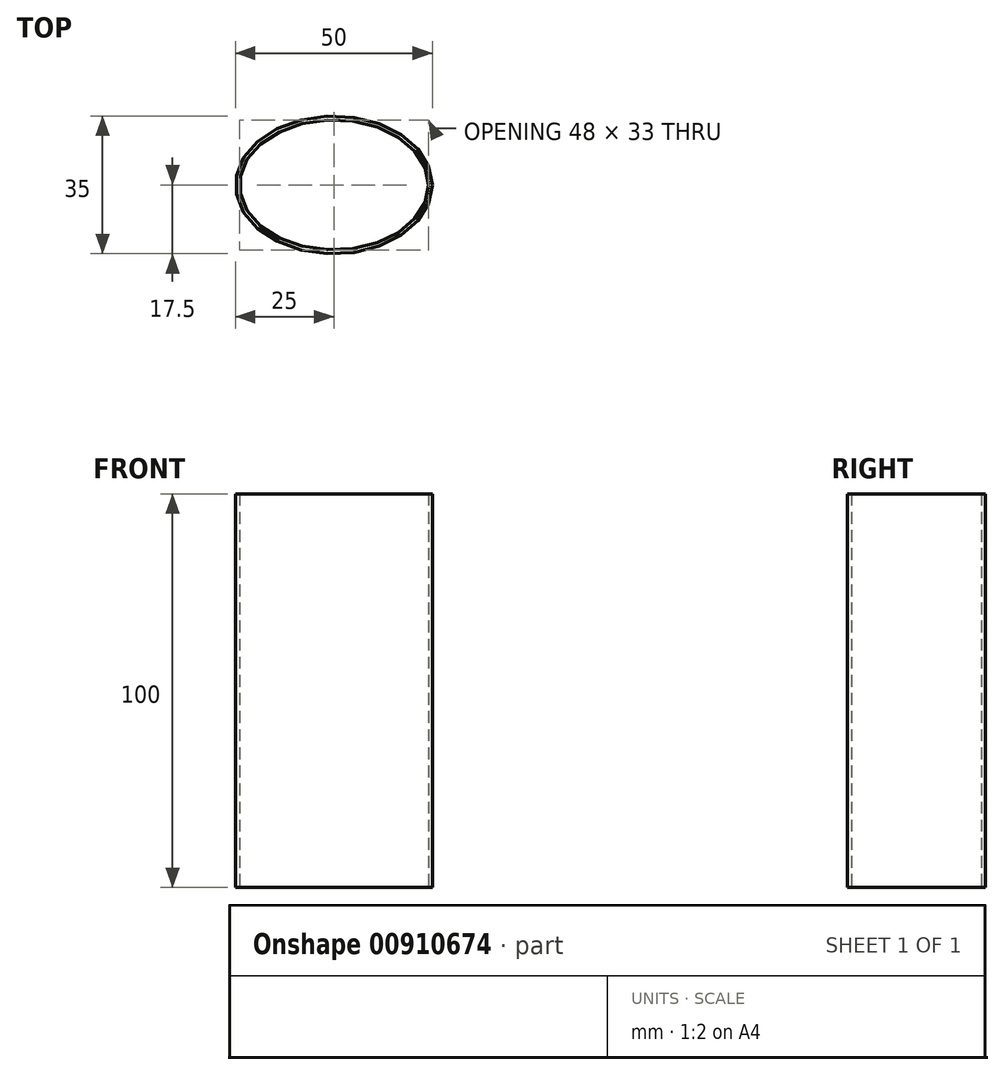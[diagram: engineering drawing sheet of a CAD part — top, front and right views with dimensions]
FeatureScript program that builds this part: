
annotation { "Feature Type Name" : "Feature", "Feature Type Description" : "" }
export const myFeature = defineFeature(function(context is Context, id is Id, definition is map)
    precondition{}
    {
        {
            var Q0;
            Q0=qCreatedBy(makeId("Top.planeOp"),FACE);
            var sketch = newSketch(context, id + "F0", { "sketchPlane" : qUnion([Q0])});
            skEllipse(sketch, "E0", {"center": v(0, 0) * mm, "majorRadius": 25 * mm, "minorRadius": 17.5 * mm, "majorAxis": v(1, 0)});
            skEllipse(sketch, "E1", {"center": v(0, 0) * mm, "majorRadius": 24 * mm, "minorRadius": 16.5 * mm, "majorAxis": v(1, 0)});
            skSolve(sketch);
        }
        {
            var Q0;
            Q0=makeQuery(id+"F0.imprint","IMPRINT",FACE,{"disambiguationData":[TD([[makeQuery(id+"F0.imprint","IMPRINT",EDGE,{"derivedFrom":sQuery(id+"F0.wireOp",EDGE,"E0")}),1.0]])]});
            extrude(context, id + "F1", {"entities" : qUnion([Q0]), "depth" : 100 * mm, "offsetDistance" : 25 * mm});
        }
    });
